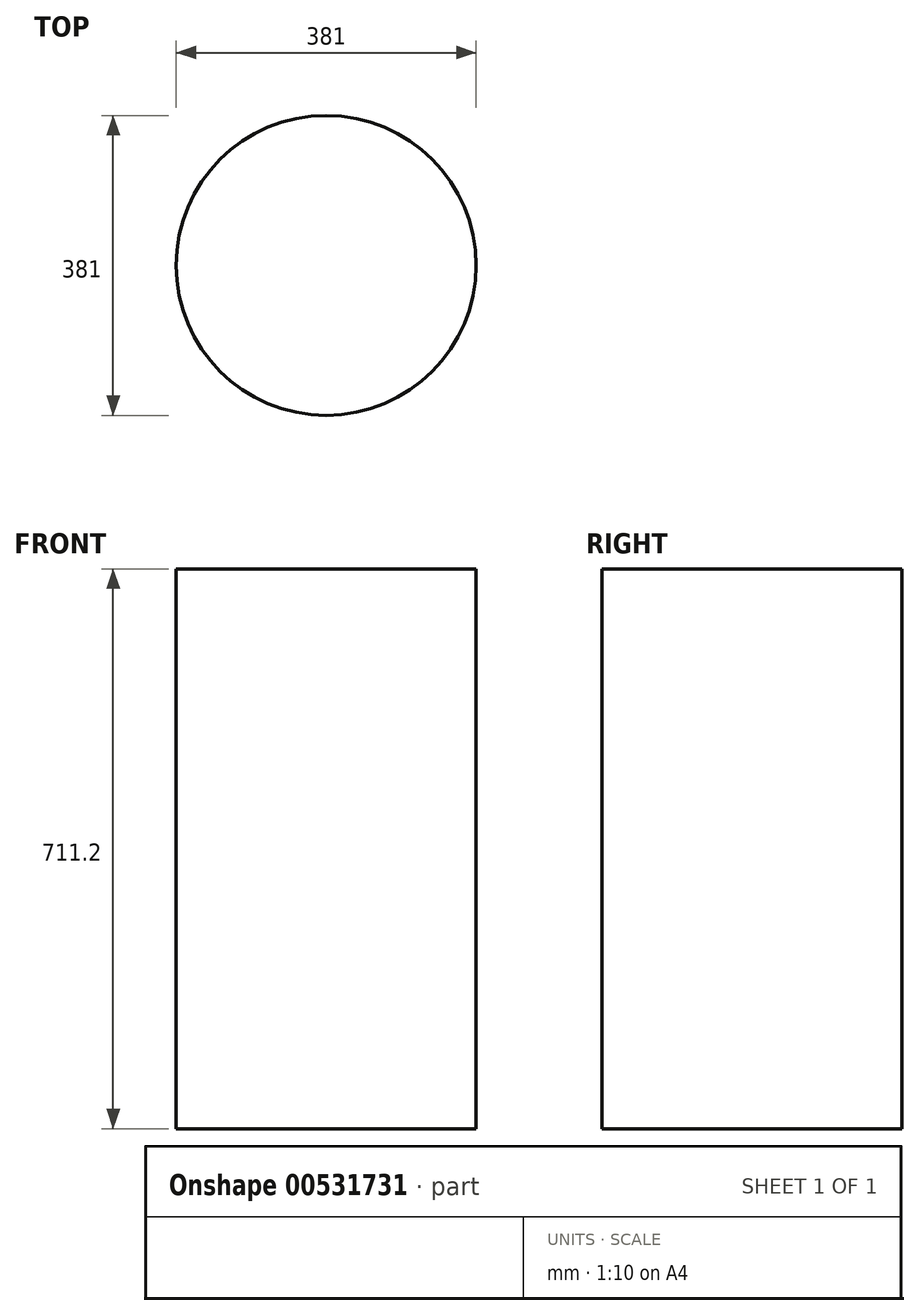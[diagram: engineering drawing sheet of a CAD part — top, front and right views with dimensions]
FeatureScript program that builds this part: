
annotation { "Feature Type Name" : "Feature", "Feature Type Description" : "" }
export const myFeature = defineFeature(function(context is Context, id is Id, definition is map)
    precondition{}
    {
        {
            var Q0;
            Q0=qCreatedBy(makeId("Top.planeOp"),FACE);
            var sketch = newSketch(context, id + "F0", { "sketchPlane" : qUnion([Q0])});
            skCircle(sketch, "E0", {"center": v(0, 0) * mm, "radius": 190.5 * mm});
            skSolve(sketch);
        }
        {
            var Q0;
            Q0=makeQuery(id+"F0.imprint","IMPRINT",FACE,{"disambiguationData":[TD([[makeQuery(id+"F0.imprint","IMPRINT",EDGE,{"derivedFrom":sQuery(id+"F0.wireOp",EDGE,"E0")}),1.0]])]});
            extrude(context, id + "F1", {"entities" : qUnion([Q0]), "depth" : 711.2 * mm, "offsetDistance" : 25.4 * mm});
        }
    });
